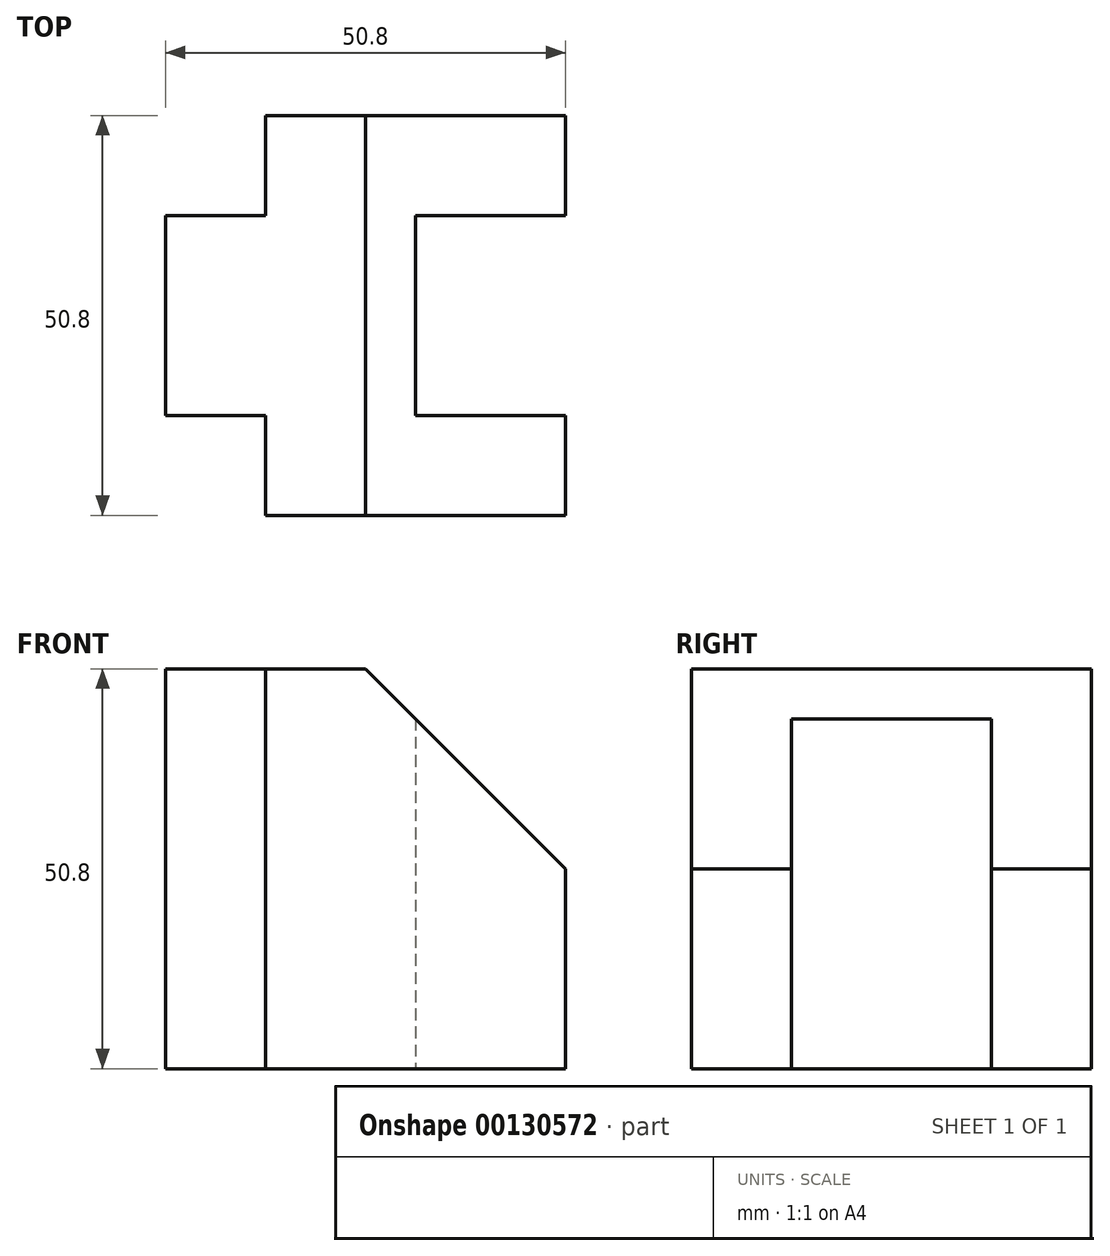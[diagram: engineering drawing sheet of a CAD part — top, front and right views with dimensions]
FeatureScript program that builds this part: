
annotation { "Feature Type Name" : "Feature", "Feature Type Description" : "" }
export const myFeature = defineFeature(function(context is Context, id is Id, definition is map)
    precondition{}
    {
        {
            var Q0;
            Q0=qCreatedBy(makeId("Top.planeOp"),FACE);
            var sketch = newSketch(context, id + "F0", { "sketchPlane" : qUnion([Q0])});
            skLineSegment(sketch, "E0", {"start": v(0, 0) * mm, "end": v(0, 12.7) * mm});
            skLineSegment(sketch, "E1", {"start": v(0, 12.7) * mm, "end": v(-12.7, 12.7) * mm});
            skLineSegment(sketch, "E2", {"start": v(-12.7, 12.7) * mm, "end": v(-12.7, 38.1) * mm});
            skLineSegment(sketch, "E3", {"start": v(-12.7, 38.1) * mm, "end": v(0, 38.1) * mm});
            skLineSegment(sketch, "E4", {"start": v(0, 38.1) * mm, "end": v(0, 50.8) * mm});
            skLineSegment(sketch, "E5", {"start": v(0, 50.8) * mm, "end": v(38.1, 50.8) * mm});
            skLineSegment(sketch, "E6", {"start": v(38.1, 50.8) * mm, "end": v(38.1, 38.1) * mm});
            skLineSegment(sketch, "E7", {"start": v(38.1, 38.1) * mm, "end": v(19.05, 38.1) * mm});
            skLineSegment(sketch, "E8", {"start": v(19.05, 38.1) * mm, "end": v(19.05, 12.7) * mm});
            skLineSegment(sketch, "E9", {"start": v(19.05, 12.7) * mm, "end": v(38.1, 12.7) * mm});
            skLineSegment(sketch, "E10", {"start": v(38.1, 12.7) * mm, "end": v(38.1, 0) * mm});
            skLineSegment(sketch, "E11", {"start": v(12.7, 0) * mm, "end": v(12.7, 50.8) * mm});
            skLineSegment(sketch, "E12", {"start": v(0, 0) * mm, "end": v(38.1, 0) * mm});
            skSolve(sketch);
        }
        {
            var Q0;
            {var subQ0=sQuery(id+"F0.wireOp",EDGE,"E0");Q0=makeQuery(id+"F0.imprint","IMPRINT",FACE,{"disambiguationData":[TD([[makeQuery(id+"F0.imprint","IMPRINT",EDGE,{"derivedFrom":subQ0}),-1.0]])]});}
            extrude(context, id + "F1", {"entities" : qUnion([Q0]), "depth" : 50.8 * mm});
        }
        {
            var Q0;
            {var subQ0=sQuery(id+"F0.wireOp",EDGE,"E6");Q0=makeQuery(id+"F0.imprint","IMPRINT",FACE,{"disambiguationData":[TD([[makeQuery(id+"F0.imprint","IMPRINT",EDGE,{"derivedFrom":subQ0}),-1.0]])]});}
            extrude(context, id + "F2", {"entities" : qUnion([Q0]), "operationType" : NewBodyOperationType.ADD, "depth" : 50.8 * mm});
        }
        {
            var Q0;
            Q0=qCreatedBy(makeId("Front.planeOp"),FACE);
            var sketch = newSketch(context, id + "F3", { "sketchPlane" : qUnion([Q0])});
            skLineSegment(sketch, "E13", {"start": v(0, 0) * mm, "end": v(-12.7, 0) * mm});
            skLineSegment(sketch, "E14", {"start": v(-12.7, 0) * mm, "end": v(-12.7, 50.8) * mm});
            skLineSegment(sketch, "E15", {"start": v(-12.7, 50.8) * mm, "end": v(0, 50.8) * mm});
            skLineSegment(sketch, "E16", {"start": v(0, 50.8) * mm, "end": v(0, 0) * mm});
            skLineSegment(sketch, "E17", {"start": v(38.1, 0) * mm, "end": v(38.1, 25.4) * mm});
            skLineSegment(sketch, "E18", {"start": v(38.1, 25.4) * mm, "end": v(12.7, 50.8) * mm});
            skLineSegment(sketch, "E19", {"start": v(12.7, 50.8) * mm, "end": v(0, 50.8) * mm});
            skLineSegment(sketch, "E20", {"start": v(0, 0) * mm, "end": v(38.1, 0) * mm});
            skLineSegment(sketch, "E21", {"start": v(12.7, 50.8) * mm, "end": v(38.1, 50.8) * mm});
            skLineSegment(sketch, "E22", {"start": v(38.1, 50.8) * mm, "end": v(38.1, 25.4) * mm});
            skLineSegment(sketch, "E23", {"start": v(19.05, 44.45) * mm, "end": v(19.05, 0) * mm, "construction": true});
            skSolve(sketch);
        }
        {
            var Q0;
            Q0=makeQuery(id+"F3.imprint","IMPRINT",FACE,{"disambiguationData":[TD([[makeQuery(id+"F3.imprint","IMPRINT",EDGE,{"derivedFrom":sQuery(id+"F3.wireOp",EDGE,"E18")}),-1.0]])]});
            extrude(context, id + "F4", {"entities" : qUnion([Q0]), "operationType" : NewBodyOperationType.REMOVE, "endBound" : BoundingType.THROUGH_ALL, "oppositeDirection" : true, "depth" : 25.4 * mm});
        }
    });
